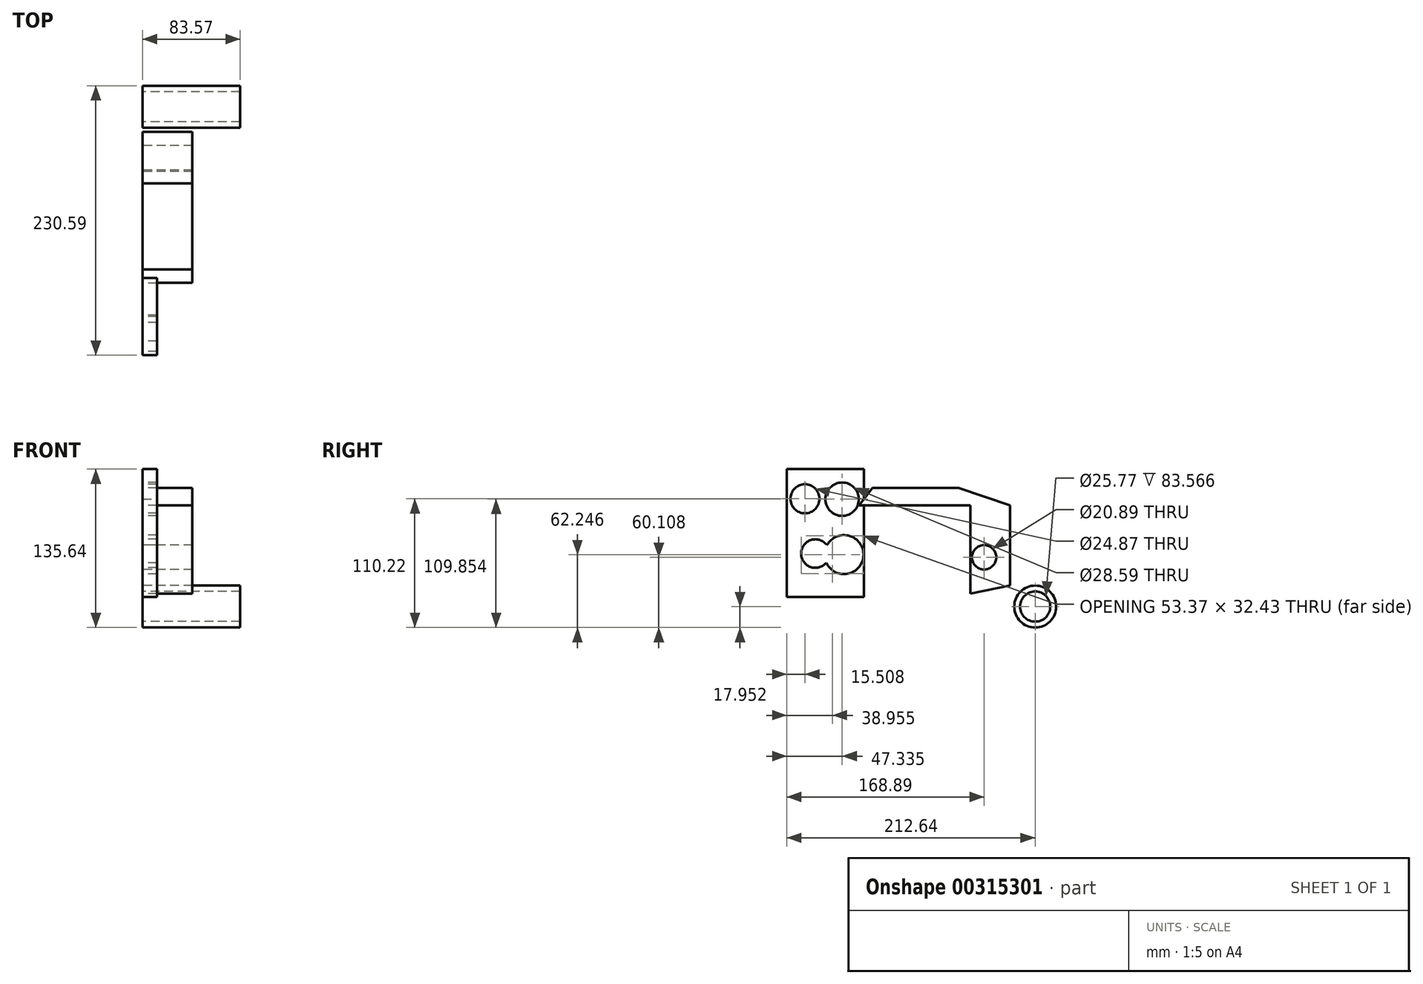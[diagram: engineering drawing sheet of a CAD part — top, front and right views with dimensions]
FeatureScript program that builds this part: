
annotation { "Feature Type Name" : "Feature", "Feature Type Description" : "" }
export const myFeature = defineFeature(function(context is Context, id is Id, definition is map)
    precondition{}
    {
        {
            var Q0;
            Q0=qCreatedBy(makeId("Right.planeOp"),FACE);
            var sketch = newSketch(context, id + "F0", { "sketchPlane" : qUnion([Q0])});
            skLineSegment(sketch, "E0", {"start": v(33.92, -55) * mm, "end": v(33.92, 13.53) * mm});
            skLineSegment(sketch, "E1", {"start": v(33.92, 13.53) * mm, "end": v(-10.28, 28.27) * mm});
            skLineSegment(sketch, "E2", {"start": v(-10.28, 28.27) * mm, "end": v(-83.95, 28.27) * mm});
            skLineSegment(sketch, "E3", {"start": v(-83.95, 28.27) * mm, "end": v(-95.26, 13.53) * mm});
            skLineSegment(sketch, "E4", {"start": v(-95.26, 13.53) * mm, "end": v(-40.43, 13.53) * mm});
            skLineSegment(sketch, "E5", {"start": v(-40.43, 13.53) * mm, "end": v(0, 13.53) * mm});
            skLineSegment(sketch, "E6", {"start": v(0, 13.53) * mm, "end": v(0, -10.8) * mm});
            skLineSegment(sketch, "E7", {"start": v(0, -10.8) * mm, "end": v(0, -62.2) * mm});
            skLineSegment(sketch, "E8", {"start": v(0, -62.2) * mm, "end": v(33.92, -55) * mm});
            skCircle(sketch, "E9", {"center": v(11.65, -31.01) * mm, "radius": 6.85 * mm});
            skCircle(sketch, "E10", {"center": v(11.65, -31.01) * mm, "radius": 10.44 * mm});
            skSolve(sketch);
        }
        {
            var Q0;
            Q0 = qSketchRegion(id + "F0", true);
            extrude(context, id + "F1", {"entities" : qUnion([Q0]), "depth" : 42.67 * mm});
        }
        {
            var Q0;
            Q0=qCreatedBy(makeId("Right.planeOp"),FACE);
            var sketch = newSketch(context, id + "F2", { "sketchPlane" : qUnion([Q0])});
            skLineSegment(sketch, "E11.bottom", {"start": v(-157.24, 44.52) * mm, "end": v(-91.14, 44.52) * mm});
            skLineSegment(sketch, "E11.top", {"start": v(-157.24, -64.86) * mm, "end": v(-91.14, -64.86) * mm});
            skLineSegment(sketch, "E11.left", {"start": v(-157.24, 44.52) * mm, "end": v(-157.24, -64.86) * mm});
            skLineSegment(sketch, "E11.right", {"start": v(-91.14, 44.52) * mm, "end": v(-91.14, -64.86) * mm});
            skCircle(sketch, "E12", {"center": v(-132.76, -27.8) * mm, "radius": 12.22 * mm});
            skCircle(sketch, "E13", {"center": v(-141.73, 19.1) * mm, "radius": 12.43 * mm});
            skCircle(sketch, "E14", {"center": v(-109.9, 18.73) * mm, "radius": 14.3 * mm});
            skCircle(sketch, "E15", {"center": v(-108.27, -28.73) * mm, "radius": 16.68 * mm});
            skSolve(sketch);
        }
        {
            var Q0;
            Q0 = qSketchRegion(id + "F2", true);
            extrude(context, id + "F3", {"entities" : qUnion([Q0]), "operationType" : NewBodyOperationType.ADD, "depth" : 12.45 * mm});
        }
        {
            var Q0;
            Q0=qCreatedBy(makeId("Right.planeOp"),FACE);
            var sketch = newSketch(context, id + "F4", { "sketchPlane" : qUnion([Q0])});
            skCircle(sketch, "E16", {"center": v(55.4, -73.17) * mm, "radius": 12.89 * mm});
            skCircle(sketch, "E17", {"center": v(55.4, -73.17) * mm, "radius": 17.95 * mm});
            skSolve(sketch);
        }
        {
            var Q0;
            Q0 = qSketchRegion(id + "F4", true);
            extrude(context, id + "F5", {"entities" : qUnion([Q0]), "depth" : 83.57 * mm});
        }
    });
